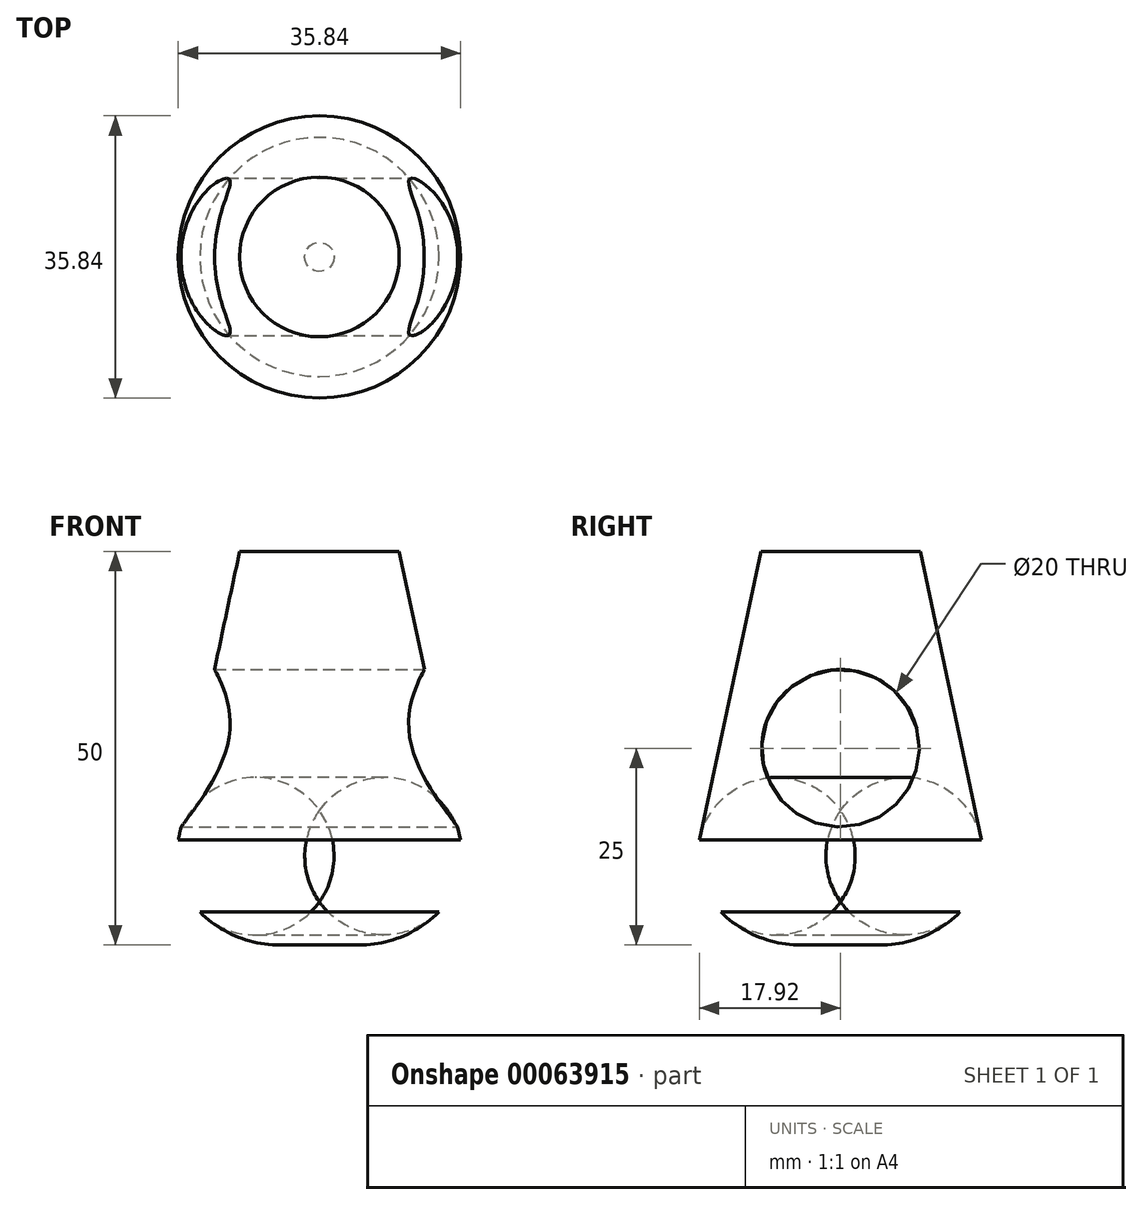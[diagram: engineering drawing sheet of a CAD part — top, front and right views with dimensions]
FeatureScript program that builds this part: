
annotation { "Feature Type Name" : "Feature", "Feature Type Description" : "" }
export const myFeature = defineFeature(function(context is Context, id is Id, definition is map)
    precondition{}
    {
        {
            var Q0;
            Q0=qCreatedBy(makeId("Right.planeOp"),FACE);
            var sketch = newSketch(context, id + "F0", { "sketchPlane" : qUnion([Q0])});
            skLineSegment(sketch, "E0", {"start": v(0, 0) * mm, "end": v(0, 25) * mm});
            skLineSegment(sketch, "E1", {"start": v(0, 0) * mm, "end": v(0, -25) * mm});
            skLineSegment(sketch, "E2", {"start": v(0, -25) * mm, "end": v(5, -25) * mm});
            skArc(sketch, "E3", {"start": v(5, -25) * mm, "mid": v(10.5, -23.9) * mm, "end": v(15.18, -20.8) * mm});
            skLineSegment(sketch, "E4", {"start": v(17.92, -11.62) * mm, "end": v(10.14, 25) * mm});
            skLineSegment(sketch, "E5", {"start": v(10.14, 25) * mm, "end": v(0, 25) * mm});
            skPoint(sketch, "E6.visualSharp", {"position": v(18.68, -15.21) * mm});
            skArc(sketch, "E6.filletArc", {"start": v(15.18, -20.8) * mm, "mid": v(17.72, -16.56) * mm, "end": v(17.92, -11.62) * mm});
            skSolve(sketch);
        }
        {
            var Q0;
            Q0 = qSketchRegion(id + "F0", true);
            var Q1;
            Q1=sQuery(id+"F0.wireOp",EDGE,"E0");
            revolve(context, id + "F1", {"entities" : qUnion([Q0]), "axis" : qUnion([Q1]), "revolveType" : RevolveType.FULL});
        }
        {
            var Q0;
            Q0=qCreatedBy(makeId("Right.planeOp"),FACE);
            cPlane(context, id + "F2", {"entities" : qUnion([Q0]), "cplaneType" : CPlaneType.OFFSET, "offset" : 25 * mm, "width" : 150 * mm, "height" : 150 * mm});
        }
        {
            var Q0;
            Q0=qCreatedBy(id+"F2.planeOp",FACE);
            var sketch = newSketch(context, id + "F3", { "sketchPlane" : qUnion([Q0])});
            skCircle(sketch, "E7", {"center": v(0, 0) * mm, "radius": 10 * mm});
            skSolve(sketch);
        }
        {
            var Q0;
            Q0=makeQuery(id+"F3.imprint","IMPRINT",FACE,{"disambiguationData":[TD([[makeQuery(id+"F3.imprint","IMPRINT",EDGE,{"derivedFrom":sQuery(id+"F3.wireOp",EDGE,"E7")}),1.0]])]});
            extrude(context, id + "F4", {"entities" : qUnion([Q0]), "operationType" : NewBodyOperationType.REMOVE, "endBound" : BoundingType.THROUGH_ALL, "oppositeDirection" : true, "depth" : 25 * mm});
        }
    });
